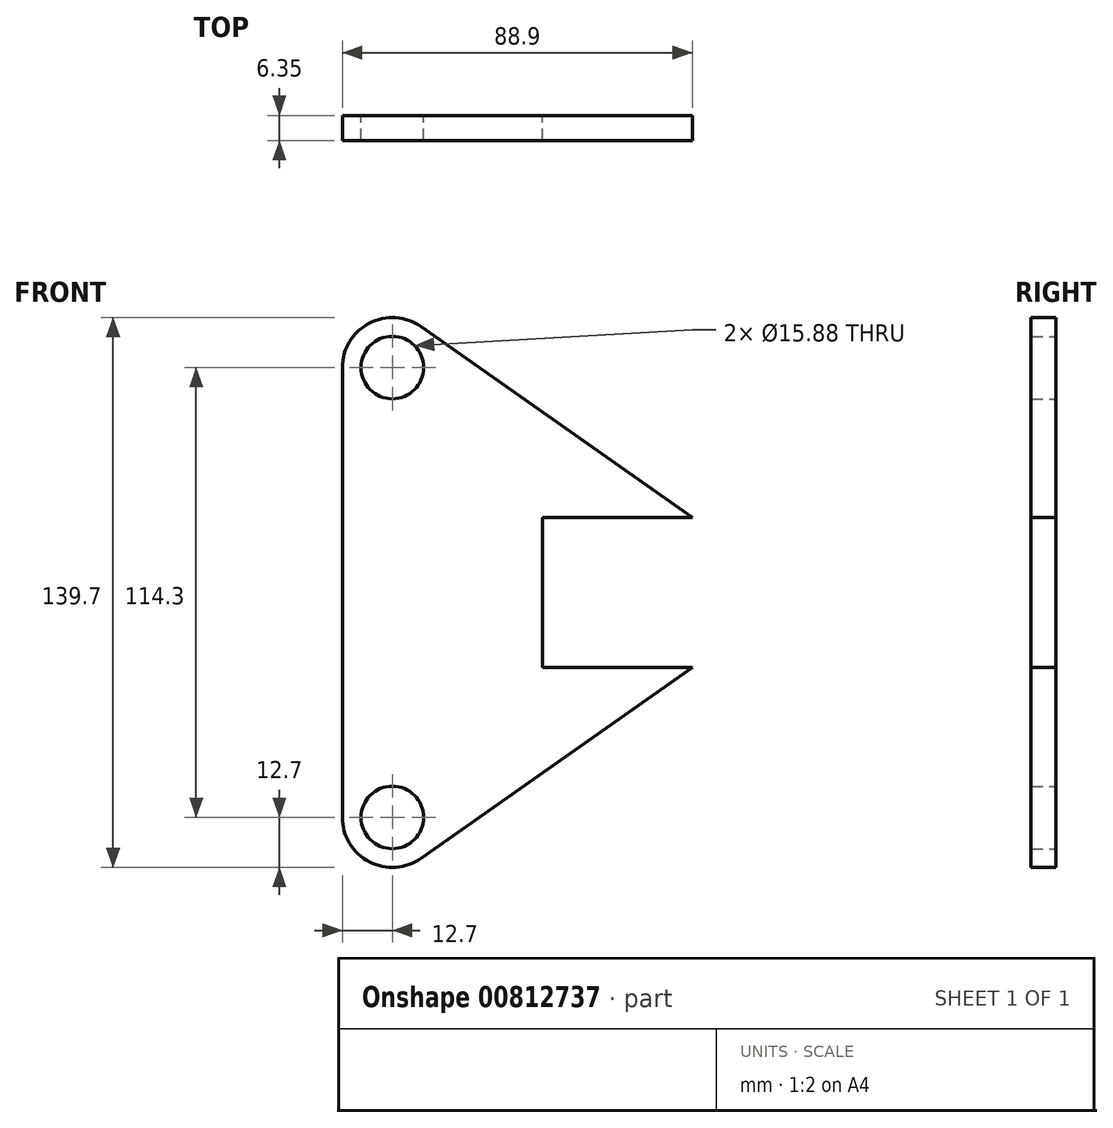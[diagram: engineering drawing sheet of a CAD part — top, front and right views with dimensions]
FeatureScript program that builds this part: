
annotation { "Feature Type Name" : "Feature", "Feature Type Description" : "" }
export const myFeature = defineFeature(function(context is Context, id is Id, definition is map)
    precondition{}
    {
        {
            var Q0;
            Q0=qCreatedBy(makeId("Front.planeOp"),FACE);
            var sketch = newSketch(context, id + "F0", { "sketchPlane" : qUnion([Q0])});
            skCircle(sketch, "E0", {"center": v(0, 0) * mm, "radius": 7.94 * mm});
            skCircle(sketch, "E1", {"center": v(0, -114.3) * mm, "radius": 7.94 * mm});
            skCircle(sketch, "E2", {"center": v(0, 0) * mm, "radius": 12.7 * mm});
            skCircle(sketch, "E3", {"center": v(0, -114.3) * mm, "radius": 12.7 * mm});
            skLineSegment(sketch, "E4", {"start": v(-12.7, 0) * mm, "end": v(-12.7, -114.3) * mm});
            skLineSegment(sketch, "E5", {"start": v(38.1, -38.1) * mm, "end": v(38.1, -76.2) * mm});
            skLineSegment(sketch, "E6", {"start": v(38.1, -76.2) * mm, "end": v(76.2, -76.2) * mm});
            skLineSegment(sketch, "E7", {"start": v(76.2, -38.1) * mm, "end": v(38.1, -38.1) * mm});
            skLineSegment(sketch, "E8", {"start": v(76.2, -38.1) * mm, "end": v(7.3, 10.39) * mm});
            skLineSegment(sketch, "E9", {"start": v(76.2, -76.2) * mm, "end": v(7.3, -124.69) * mm});
            skPoint(sketch, "E10.startSnap0", {"position": v(57.15, -76.2) * mm});
            skPoint(sketch, "E10.start.orphan", {"position": v(57.15, -89.6) * mm});
            skPoint(sketch, "E11.end.orphan", {"position": v(38.1, -57.15) * mm});
            skPoint(sketch, "E11.start.orphan", {"position": v(-12.7, -57.15) * mm});
            skSolve(sketch);
        }
        {
            var Q0;
            Q0 = qSketchRegion(id + "F0", true);
            extrude(context, id + "F1", {"entities" : qUnion([Q0]), "depth" : 6.35 * mm, "offsetDistance" : 25.4 * mm});
        }
    });
